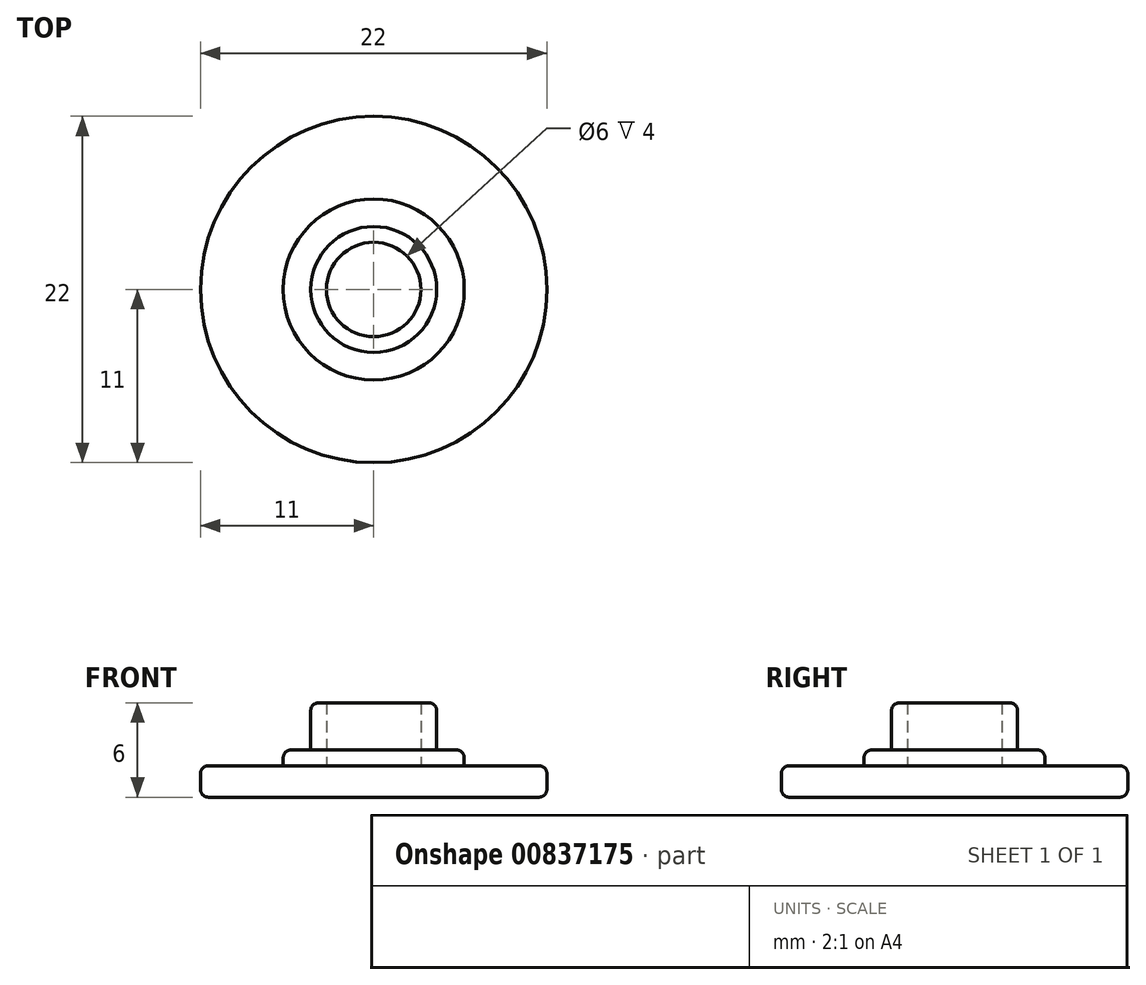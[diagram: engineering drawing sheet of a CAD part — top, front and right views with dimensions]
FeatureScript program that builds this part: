
annotation { "Feature Type Name" : "Feature", "Feature Type Description" : "" }
export const myFeature = defineFeature(function(context is Context, id is Id, definition is map)
    precondition{}
    {
        {
            var Q0;
            Q0=qCreatedBy(makeId("Top.planeOp"),FACE);
            var sketch = newSketch(context, id + "F0", { "sketchPlane" : qUnion([Q0])});
            skCircle(sketch, "E0", {"center": v(0, 0) * mm, "radius": 4 * mm});
            skCircle(sketch, "E1", {"center": v(0, 0) * mm, "radius": 5.75 * mm});
            skCircle(sketch, "E2", {"center": v(0, 0) * mm, "radius": 11 * mm});
            skCircle(sketch, "E3", {"center": v(0, 0) * mm, "radius": 3 * mm});
            skSolve(sketch);
        }
        {
            var Q0;
            Q0=makeQuery(id+"F0.imprint","IMPRINT",FACE,{"disambiguationData":[TD([[makeQuery(id+"F0.imprint","IMPRINT",EDGE,{"derivedFrom":sQuery(id+"F0.wireOp",EDGE,"E1")}),-1.0]])]});
            var Q1;
            Q1=makeQuery(id+"F0.imprint","IMPRINT",FACE,{"disambiguationData":[TD([[makeQuery(id+"F0.imprint","IMPRINT",EDGE,{"derivedFrom":sQuery(id+"F0.wireOp",EDGE,"E0")}),-1.0]])]});
            var Q2;
            Q2=makeQuery(id+"F0.imprint","IMPRINT",FACE,{"disambiguationData":[TD([[makeQuery(id+"F0.imprint","IMPRINT",EDGE,{"derivedFrom":sQuery(id+"F0.wireOp",EDGE,"E0")}),1.0]])]});
            var Q3;
            Q3=makeQuery(id+"F0.imprint","IMPRINT",FACE,{"disambiguationData":[TD([[makeQuery(id+"F0.imprint","IMPRINT",EDGE,{"derivedFrom":sQuery(id+"F0.wireOp",EDGE,"E3")}),1.0]])]});
            extrude(context, id + "F1", {"entities" : qUnion([Q0, Q1, Q2, Q3]), "depth" : 2 * mm, "offsetDistance" : 25 * mm});
        }
        {
            var Q0;
            Q0=makeQuery(id+"F0.imprint","IMPRINT",FACE,{"disambiguationData":[TD([[makeQuery(id+"F0.imprint","IMPRINT",EDGE,{"derivedFrom":sQuery(id+"F0.wireOp",EDGE,"E0")}),-1.0]])]});
            extrude(context, id + "F2", {"entities" : qUnion([Q0]), "operationType" : NewBodyOperationType.ADD, "depth" : 3 * mm, "offsetDistance" : 25 * mm});
        }
        {
            var Q0;
            Q0=makeQuery(id+"F0.imprint","IMPRINT",FACE,{"disambiguationData":[TD([[makeQuery(id+"F0.imprint","IMPRINT",EDGE,{"derivedFrom":sQuery(id+"F0.wireOp",EDGE,"E0")}),1.0]])]});
            extrude(context, id + "F3", {"entities" : qUnion([Q0]), "operationType" : NewBodyOperationType.ADD, "depth" : 6 * mm, "offsetDistance" : 25 * mm});
        }
        {
            var Q0;
            Q0=makeQuery(id+"F3.opExtrude","CAP_EDGE",EDGE,{"disambiguationData":[OSD([sQuery(id+"F0.wireOp",EDGE,"E0")])],"isStart":false});
            var Q1;
            Q1=makeQuery(id+"F2.opExtrude","CAP_EDGE",EDGE,{"disambiguationData":[OSD([sQuery(id+"F0.wireOp",EDGE,"E1")])],"isStart":false});
            var Q2;
            Q2=makeQuery(id+"F1.opExtrude","CAP_EDGE",EDGE,{"disambiguationData":[OSD([sQuery(id+"F0.wireOp",EDGE,"E2")])],"isStart":false});
            var Q3;
            Q3=makeQuery(id+"F1.opExtrude","CAP_EDGE",EDGE,{"disambiguationData":[OSD([sQuery(id+"F0.wireOp",EDGE,"E2")])],"isStart":true});
            fillet(context, id + "F4", {"entities" : qUnion([Q0, Q1, Q2, Q3]), "radius" : .5 * mm, "tangentPropagation" : true, "allowEdgeOverflow" : false});
        }
    });
